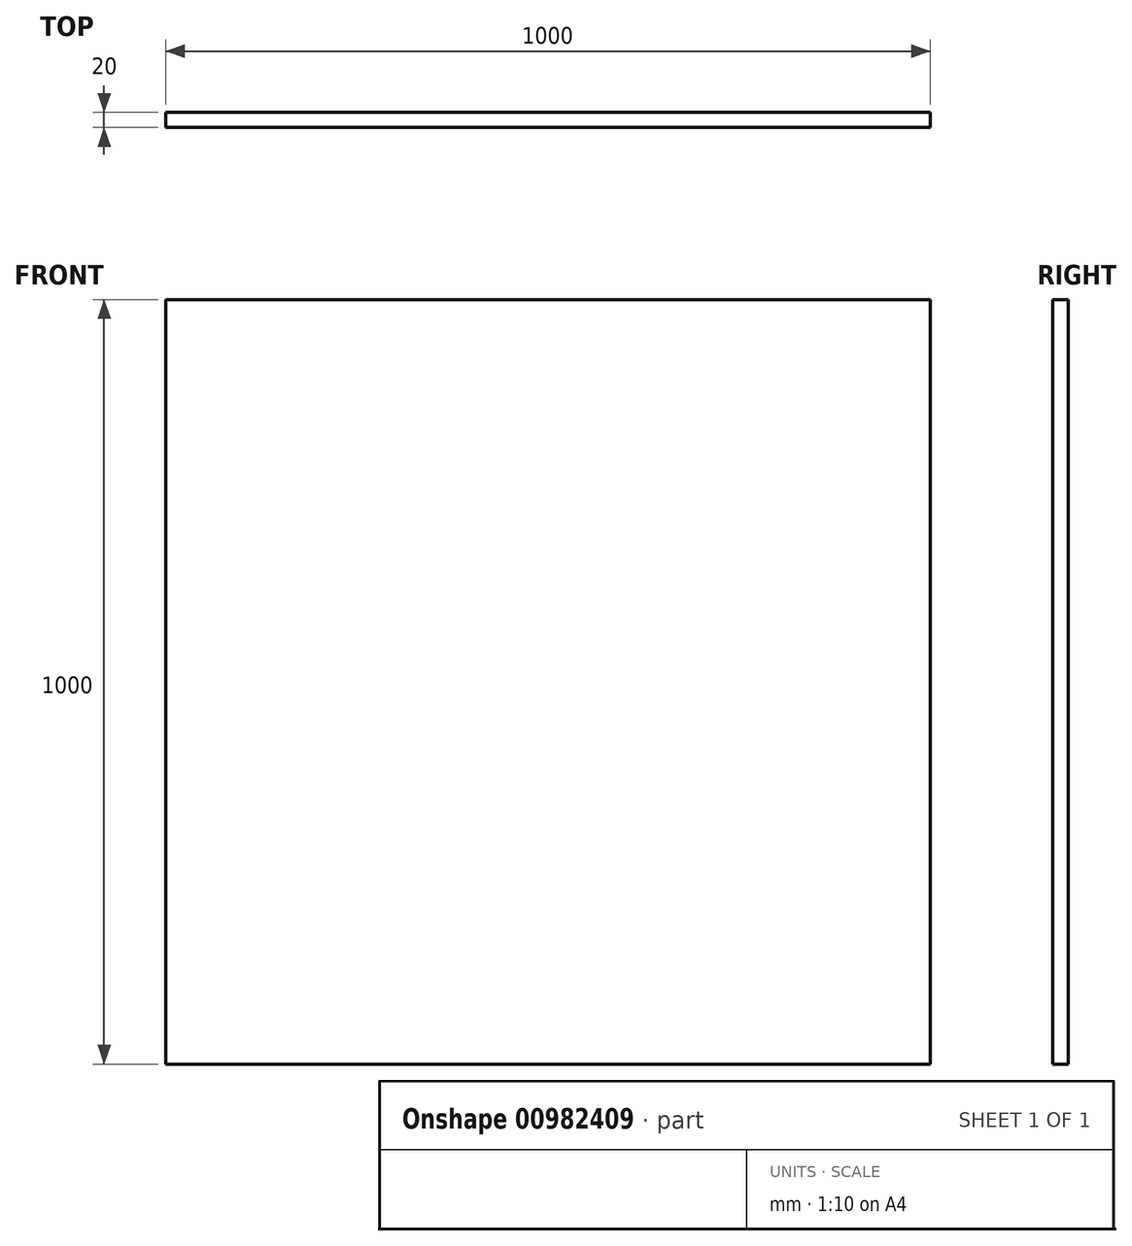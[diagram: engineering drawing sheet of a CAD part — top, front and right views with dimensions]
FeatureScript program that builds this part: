
annotation { "Feature Type Name" : "Feature", "Feature Type Description" : "" }
export const myFeature = defineFeature(function(context is Context, id is Id, definition is map)
    precondition{}
    {
        {
            var Q0;
            Q0=qCreatedBy(makeId("Front.planeOp"),FACE);
            var sketch = newSketch(context, id + "F0", { "sketchPlane" : qUnion([Q0])});
            skLineSegment(sketch, "E0.bottom", {"start": v(0, 0) * mm, "end": v(1000, 0) * mm});
            skLineSegment(sketch, "E0.top", {"start": v(0, 1000) * mm, "end": v(1000, 1000) * mm});
            skLineSegment(sketch, "E0.left", {"start": v(0, 0) * mm, "end": v(0, 1000) * mm});
            skLineSegment(sketch, "E0.right", {"start": v(1000, 0) * mm, "end": v(1000, 1000) * mm});
            skSolve(sketch);
        }
        {
            var Q0;
            Q0=makeQuery(id+"F0.imprint","IMPRINT",FACE,{"disambiguationData":[TD([[makeQuery(id+"F0.imprint","IMPRINT",EDGE,{"derivedFrom":sQuery(id+"F0.wireOp",EDGE,"E0.bottom")}),1.0]])]});
            extrude(context, id + "F1", {"entities" : qUnion([Q0]), "depth" : 20 * mm, "offsetDistance" : 25 * mm});
        }
    });
